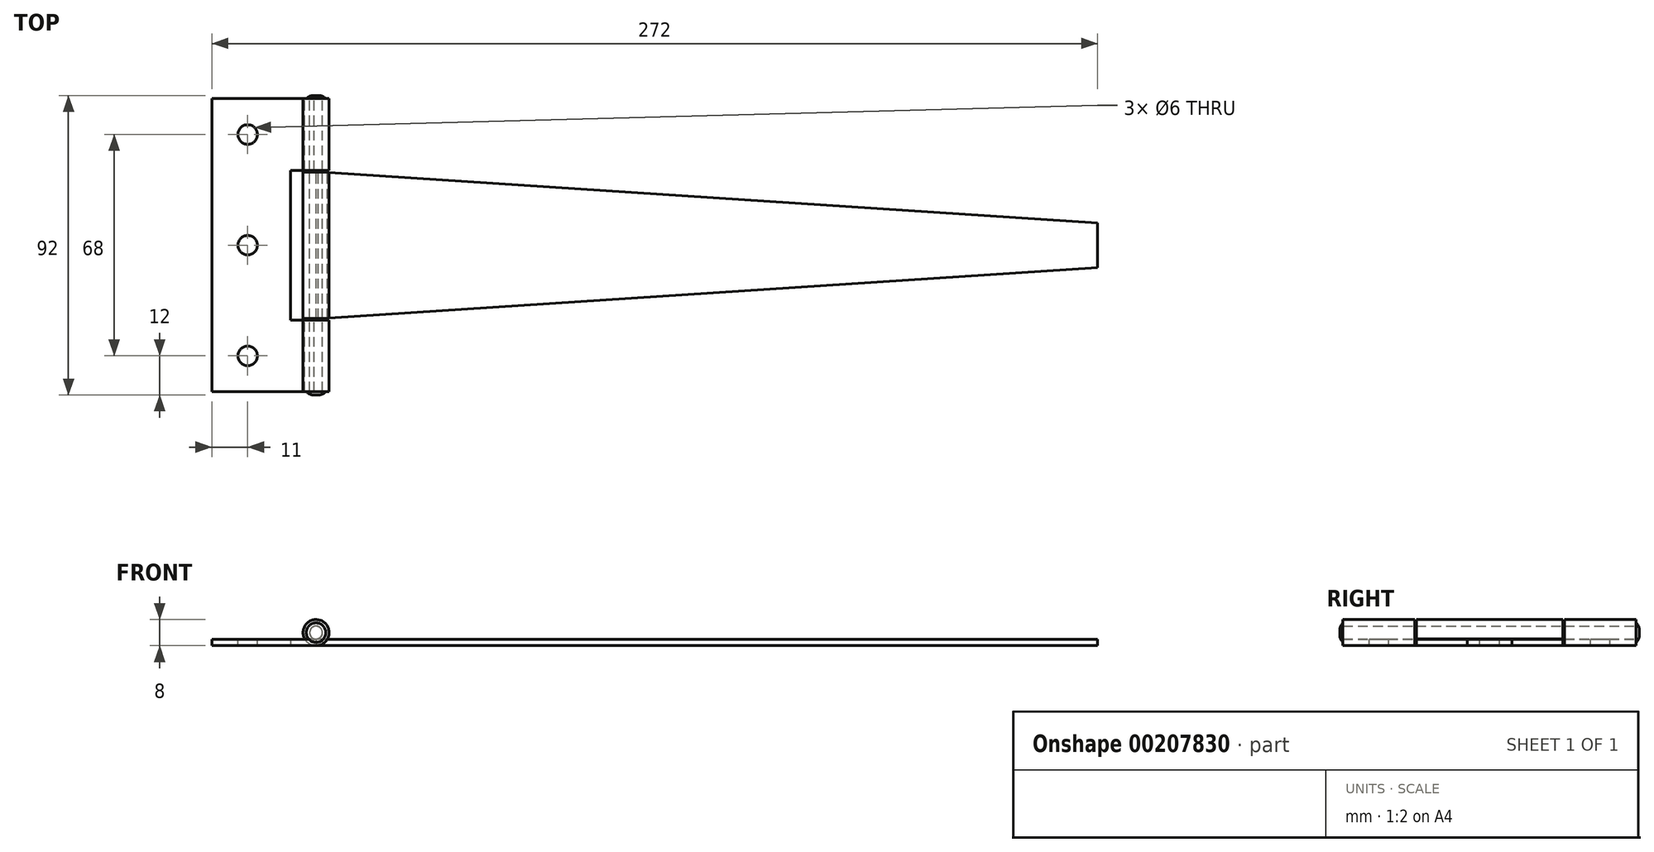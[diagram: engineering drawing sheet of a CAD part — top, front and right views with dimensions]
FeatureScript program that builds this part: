
annotation { "Feature Type Name" : "Feature", "Feature Type Description" : "" }
export const myFeature = defineFeature(function(context is Context, id is Id, definition is map)
    precondition{}
    {
        {
            assignVariable(context, id + "F0", {"name" : "Thickness", "anyValue" : 2});
        }
        {
            var Q0;
            Q0=qCreatedBy(makeId("Front.planeOp"),FACE);
            var sketch = newSketch(context, id + "F1", { "sketchPlane" : qUnion([Q0])});
            skLineSegment(sketch, "E0", {"start": v(0, 0) * mm, "end": v(32, 0) * mm});
            skArc(sketch, "E1", {"start": v(32, 0) * mm, "mid": v(34.05, 7.44) * mm, "end": v(28.48, 2.1) * mm});
            skLineSegment(sketch, "E2", {"start": v(0, 0) * mm, "end": v(0, 2) * mm});
            skLineSegment(sketch, "E3", {"start": v(0, 2) * mm, "end": v(32, 2) * mm});
            skArc(sketch, "E4", {"start": v(32, 2) * mm, "mid": v(32.32, 5.97) * mm, "end": v(31.38, 2.1) * mm});
            skLineSegment(sketch, "E5", {"start": v(28.48, 2.1) * mm, "end": v(31.38, 2.1) * mm});
            skSolve(sketch);
        }
        {
            var Q0;
            Q0 = qSketchRegion(id + "F1", true);
            extrude(context, id + "F2", {"entities" : qUnion([Q0]), "depth" : 90 * mm});
        }
        {
            var Q0;
            Q0=makeQuery(id+"F2.opExtrude","SWEPT_FACE",FACE,{"disambiguationData":[OSD([sQuery(id+"F1.wireOp",EDGE,"E3")])]});
            var sketch = newSketch(context, id + "F3", { "sketchPlane" : qUnion([Q0])});
            skLineSegment(sketch, "E6.bottom", {"start": v(24.2, -22) * mm, "end": v(92.17, -22) * mm});
            skLineSegment(sketch, "E6.top", {"start": v(24.2, -68) * mm, "end": v(92.17, -68) * mm});
            skLineSegment(sketch, "E6.left", {"start": v(24.2, -22) * mm, "end": v(24.2, -68) * mm});
            skLineSegment(sketch, "E6.right", {"start": v(92.17, -22) * mm, "end": v(92.17, -68) * mm});
            skSolve(sketch);
        }
        {
            var Q0;
            Q0 = qSketchRegion(id + "F3", true);
            extrude(context, id + "F4", {"entities" : qUnion([Q0]), "operationType" : NewBodyOperationType.REMOVE, "endBound" : BoundingType.SYMMETRIC, "depth" : 25 * mm});
        }
        {
            var Q0;
            Q0=makeQuery(id+"F2.opExtrude","SWEPT_FACE",FACE,{"disambiguationData":[OSD([sQuery(id+"F1.wireOp",EDGE,"E3")])]});
            var sketch = newSketch(context, id + "F5", { "sketchPlane" : qUnion([Q0])});
            skPoint(sketch, "E7", {"position": v(11, -11) * mm});
            skPoint(sketch, "E8.0.1.0", {"position": v(11, -45) * mm});
            skPoint(sketch, "E8.0.2.0", {"position": v(11, -79) * mm});
            skLineSegment(sketch, "E8.direction1", {"start": v(11, -11) * mm, "end": v(36, -11) * mm, "construction": true});
            skLineSegment(sketch, "E8.direction2", {"start": v(11, -11) * mm, "end": v(11, -45) * mm, "construction": true});
            skSolve(sketch);
        }
        {
            var Q0;
            Q0=sQuery(id+"F5.wireOp",VERTEX,"E7");
            var Q1;
            Q1=sQuery(id+"F5.wireOp",VERTEX,"E8.0.1.0");
            var Q2;
            Q2=sQuery(id+"F5.wireOp",VERTEX,"E8.0.2.0");
            var Q3;
            Q3=makeQuery(id+"F2.opExtrude","SWEPT_BODY",BODY,{"disambiguationData":[OSD([sQuery(id+"F1.wireOp",EDGE,"E0"),sQuery(id+"F1.wireOp",EDGE,"E1"),sQuery(id+"F1.wireOp",EDGE,"E2"),sQuery(id+"F1.wireOp",EDGE,"E3"),sQuery(id+"F1.wireOp",EDGE,"E4"),sQuery(id+"F1.wireOp",EDGE,"E5")])]});
            hole(context, id + "F6", {"style" : HoleStyle.SIMPLE, "endStyle" : HoleEndStyle.THROUGH, "holeDiameter" : 6 * mm, "locations" : qUnion([Q0, Q1, Q2]), "scope" : qUnion([Q3]), "isTappedThrough" : true});
        }
        {
            var Q0;
            Q0=qCreatedBy(makeId("Front.planeOp"),FACE);
            var sketch = newSketch(context, id + "F7", { "sketchPlane" : qUnion([Q0])});
            skCircle(sketch, "E9", {"center": v(32, 4) * mm, "radius": 1.95 * mm});
            skSolve(sketch);
        }
        {
            var Q0;
            Q0 = qSketchRegion(id + "F7", true);
            extrude(context, id + "F8", {"entities" : qUnion([Q0]), "depth" : 90 * mm});
        }
        {
            var Q0;
            Q0=makeQuery(id+"F8.opExtrude","CAP_FACE",FACE,{"disambiguationData":[OSD([sQuery(id+"F7.wireOp",EDGE,"E9")])],"isStart":true});
            var sketch = newSketch(context, id + "F9", { "sketchPlane" : qUnion([Q0])});
            skCircle(sketch, "E10", {"center": v(-32, 4) * mm, "radius": 3 * mm});
            skSolve(sketch);
        }
        {
            var Q0;
            Q0 = qSketchRegion(id + "F9", true);
            extrude(context, id + "F10", {"entities" : qUnion([Q0]), "depth" : 1 * mm});
        }
        {
            var Q0;
            Q0=makeQuery(id+"F10.opExtrude","CAP_EDGE",EDGE,{"disambiguationData":[OSD([sQuery(id+"F9.wireOp",EDGE,"E10")])],"isStart":false});
            fillet(context, id + "F11", {"entities" : qUnion([Q0]), "radius" : 3 * mm, "tangentPropagation" : true, "allowEdgeOverflow" : false});
        }
        {
            var Q0;
            Q0=makeQuery(id+"F8.opExtrude","CAP_FACE",FACE,{"disambiguationData":[OSD([sQuery(id+"F7.wireOp",EDGE,"E9")])],"isStart":false});
            var sketch = newSketch(context, id + "F12", { "sketchPlane" : qUnion([Q0])});
            skCircle(sketch, "E11", {"center": v(32, 4) * mm, "radius": 3 * mm});
            skSolve(sketch);
        }
        {
            var Q0;
            Q0 = qSketchRegion(id + "F12", true);
            extrude(context, id + "F13", {"entities" : qUnion([Q0]), "depth" : 1 * mm});
        }
        {
            var Q0;
            Q0=makeQuery(id+"F13.opExtrude","CAP_FACE",FACE,{"disambiguationData":[OSD([sQuery(id+"F12.wireOp",EDGE,"E11")])],"isStart":false});
            fillet(context, id + "F14", {"entities" : qUnion([Q0]), "radius" : 3 * mm, "tangentPropagation" : true, "allowEdgeOverflow" : false});
        }
        {
            var Q0;
            Q0=qCreatedBy(makeId("Top.planeOp"),FACE);
            var sketch = newSketch(context, id + "F15", { "sketchPlane" : qUnion([Q0])});
            skLineSegment(sketch, "E12", {"start": v(34, -22.5) * mm, "end": v(272, -38.15) * mm});
            skLineSegment(sketch, "E13", {"start": v(272, -38.15) * mm, "end": v(272, -51.85) * mm});
            skLineSegment(sketch, "E14", {"start": v(272, -51.85) * mm, "end": v(34, -67.5) * mm});
            skLineSegment(sketch, "E15", {"start": v(34, -22.5) * mm, "end": v(32, -22.5) * mm});
            skLineSegment(sketch, "E16", {"start": v(32, -22.5) * mm, "end": v(32, -67.5) * mm});
            skLineSegment(sketch, "E17", {"start": v(32, -67.5) * mm, "end": v(34, -67.5) * mm});
            skSolve(sketch);
        }
        {
            var Q0;
            Q0 = qSketchRegion(id + "F15", true);
            extrude(context, id + "F16", {"entities" : qUnion([Q0]), "depth" : (getVariable(context, 'Thickness')) * mm});
        }
        {
            var Q0;
            Q0=makeQuery(id+"F16.opExtrude","SWEPT_FACE",FACE,{"disambiguationData":[OSD([sQuery(id+"F15.wireOp",EDGE,"E15")])]});
            var sketch = newSketch(context, id + "F17", { "sketchPlane" : qUnion([Q0])});
            skPoint(sketch, "E18", {"position": v(-32, 0) * mm});
            skPoint(sketch, "E19", {"position": v(-32, 2) * mm});
            skLineSegment(sketch, "E20", {"start": v(-32, 2) * mm, "end": v(-34, 2) * mm});
            skLineSegment(sketch, "E21", {"start": v(-34, 0) * mm, "end": v(-32, 0) * mm});
            skArc(sketch, "E22", {"start": v(-32, 0) * mm, "mid": v(-29.95, 7.44) * mm, "end": v(-35.52, 2.1) * mm});
            skArc(sketch, "E23", {"start": v(-32, 2) * mm, "mid": v(-31.68, 5.97) * mm, "end": v(-32.62, 2.1) * mm});
            skLineSegment(sketch, "E24", {"start": v(-32.62, 2.1) * mm, "end": v(-35.52, 2.1) * mm});
            skLineSegment(sketch, "E25", {"start": v(-32, 2) * mm, "end": v(-32, 0) * mm});
            skSolve(sketch);
        }
        {
            var Q0;
            Q0 = qSketchRegion(id + "F17", true);
            extrude(context, id + "F18", {"entities" : qUnion([Q0]), "oppositeDirection" : true, "depth" : 45 * mm});
        }
        {
            var Q0;
            Q0=makeQuery(id+"F16.opExtrude","CAP_FACE",FACE,{"disambiguationData":[OSD([sQuery(id+"F15.wireOp",EDGE,"E12"),sQuery(id+"F15.wireOp",EDGE,"E13"),sQuery(id+"F15.wireOp",EDGE,"E14"),sQuery(id+"F15.wireOp",EDGE,"E15"),sQuery(id+"F15.wireOp",EDGE,"E16"),sQuery(id+"F15.wireOp",EDGE,"E17")])],"isStart":false});
            var sketch = newSketch(context, id + "F19", { "sketchPlane" : qUnion([Q0])});
            skPoint(sketch, "E26", {"position": v(262, -45) * mm});
            skPoint(sketch, "E27", {"position": v(197, -45) * mm});
            skPoint(sketch, "E28", {"position": v(132, -45) * mm});
            skPoint(sketch, "E29", {"position": v(65.52, -32.5) * mm});
            skPoint(sketch, "E30", {"position": v(48.52, -57.5) * mm});
            skLineSegment(sketch, "E31", {"start": v(272, -45) * mm, "end": v(-13.65, -45) * mm, "construction": true});
            skSolve(sketch);
        }
        {
            var Q0;
            Q0=sQuery(id+"F19.wireOp",VERTEX,"E30");
            var Q1;
            Q1=sQuery(id+"F19.wireOp",VERTEX,"E29");
            var Q2;
            Q2=sQuery(id+"F19.wireOp",VERTEX,"E27");
            var Q3;
            Q3=sQuery(id+"F19.wireOp",VERTEX,"E28");
            var Q4;
            Q4=sQuery(id+"F19.wireOp",VERTEX,"E26");
            var Q5;
            Q5=makeQuery(id+"F18.opExtrude","SWEPT_BODY",BODY,{"disambiguationData":[OSD([sQuery(id+"F17.wireOp",EDGE,"E22"),sQuery(id+"F17.wireOp",EDGE,"E23"),sQuery(id+"F17.wireOp",EDGE,"E24"),sQuery(id+"F17.wireOp",EDGE,"E25")])]});
            hole(context, id + "F20", {"style" : HoleStyle.SIMPLE, "endStyle" : HoleEndStyle.THROUGH, "holeDiameter" : 6 * mm, "locations" : qUnion([Q0, Q1, Q2, Q3, Q4]), "scope" : qUnion([Q5]), "isTappedThrough" : true});
        }
    });
